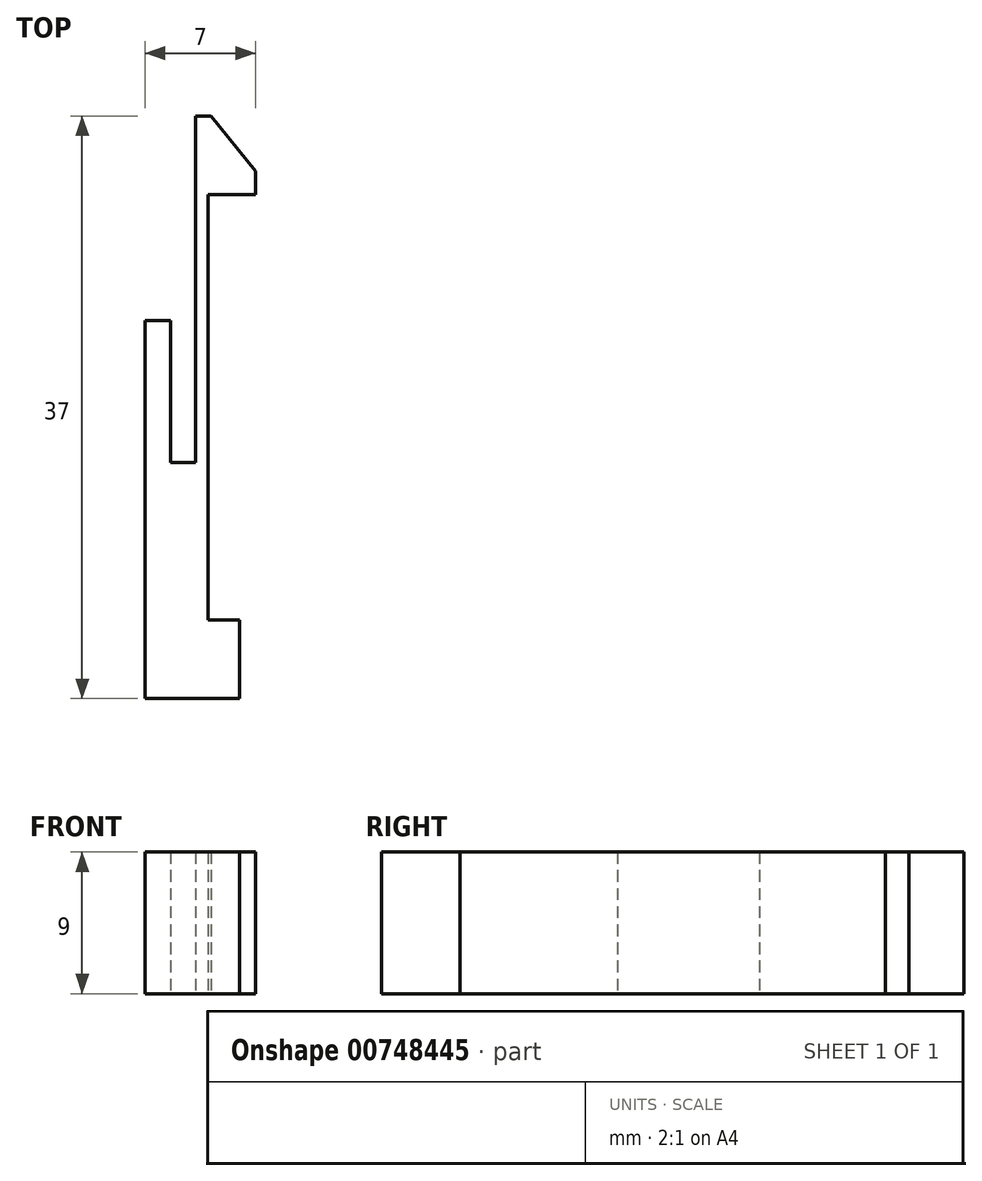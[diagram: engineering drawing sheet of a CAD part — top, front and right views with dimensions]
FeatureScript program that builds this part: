
annotation { "Feature Type Name" : "Feature", "Feature Type Description" : "" }
export const myFeature = defineFeature(function(context is Context, id is Id, definition is map)
    precondition{}
    {
        {
            var Q0;
            Q0=qCreatedBy(makeId("Top.planeOp"),FACE);
            var sketch = newSketch(context, id + "F0", { "sketchPlane" : qUnion([Q0])});
            skLineSegment(sketch, "E0", {"start": v(0, 0) * mm, "end": v(6, 0) * mm});
            skLineSegment(sketch, "E1", {"start": v(6, 0) * mm, "end": v(6, 5) * mm});
            skLineSegment(sketch, "E2", {"start": v(6, 5) * mm, "end": v(4, 5) * mm});
            skLineSegment(sketch, "E3", {"start": v(4, 5) * mm, "end": v(4, 32) * mm});
            skLineSegment(sketch, "E4", {"start": v(4, 32) * mm, "end": v(7, 32) * mm});
            skLineSegment(sketch, "E5", {"start": v(3.19, 37) * mm, "end": v(3.19, 15) * mm});
            skLineSegment(sketch, "E6", {"start": v(0, 24) * mm, "end": v(0, 0) * mm});
            skLineSegment(sketch, "E7", {"start": v(7, 32) * mm, "end": v(7, 33.5) * mm});
            skLineSegment(sketch, "E8", {"start": v(7, 33.5) * mm, "end": v(4.19, 37) * mm});
            skLineSegment(sketch, "E9", {"start": v(4.19, 37) * mm, "end": v(3.19, 37) * mm});
            skLineSegment(sketch, "E10", {"start": v(0, 24) * mm, "end": v(1.6, 24) * mm});
            skLineSegment(sketch, "E11", {"start": v(1.6, 24) * mm, "end": v(1.6, 15) * mm});
            skLineSegment(sketch, "E12", {"start": v(1.6, 15) * mm, "end": v(3.19, 15) * mm});
            skSolve(sketch);
        }
        {
            var Q0;
            Q0=makeQuery(id+"F0.imprint","IMPRINT",FACE,{"disambiguationData":[TD([[makeQuery(id+"F0.imprint","IMPRINT",EDGE,{"derivedFrom":sQuery(id+"F0.wireOp",EDGE,"E0")}),1.0]])]});
            extrude(context, id + "F1", {"entities" : qUnion([Q0]), "depth" : 9 * mm, "offsetDistance" : 25 * mm});
        }
    });
